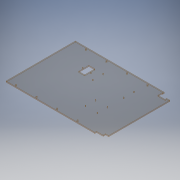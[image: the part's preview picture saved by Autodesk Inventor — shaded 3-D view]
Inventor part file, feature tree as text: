
AUTODESK INVENTOR PART (.ipt)
format: ipt  version: 2019.4 (Build 234330000, 330)  size: 210,944 bytes
history: native  units: mm
features: sketch x6, extrude x5
ambient origin geometry x8: Origin, YZ Plane, XZ Plane, XY Plane, X Axis, Y Axis, Z Axis, Center Point
bodies: Solid1 (feature_tree)
feature tree (11):
  extrude  "Extrusion1"  Depth=337.83mm
  extrude  "Extrusion2"  Depth=20.0mm
  extrude  "Extrusion3"  Depth=8.0mm
  sketch  "Sketch5"  dims[d7=90.0deg d8=12.0mm]
  extrude  "Extrusion4"  Depth=12.0mm
  extrude  "Extrusion5"  Depth=5.0mm TaperAngle=0.0deg
  sketch  "Sketch1"  dims[d0=480.0mm d1=337.83mm]
  sketch  "Sketch2"  dims[d2=5.0mm d3=0.0mm d4=20.0mm]
  sketch  "Sketch4"  dims[d5=15.0mm d6=8.0mm]
  sketch  "Sketch8"  dims[d9=32.0mm d10=5.0mm d11=0.0mm]
  sketch  "Sketch9"  dims[d14=40.0mm d15=8.732mm d16=5.5mm d17=40.0mm d19=100.0mm d20=10.0mm d22=10.0mm d24=60.0mm d25=8.732mm d26=5.5mm d27=40.0mm d29=100.0mm d30=10.0mm d32=10.0mm d34=10.0mm d35=0.0mm d36=480.0mm d37=339.0mm d38=35.0mm d39=20.0mm d40=10.0mm d41=0.0mm d42=4.0mm d43=70.0mm d44=125.0mm d45=20.0mm d47=50.0mm d48=20.0mm d50=150.0mm d53=40.0mm d54=180.0deg d55=15.0mm d56=15.0mm d57=29.0mm d58=50.0mm d59=5.5mm d60=5.5mm d61=3.5mm d62=3.5mm d63=3.5mm d64=90.0mm d65=125.0mm d66=20.0mm d68=58.0mm d69=20.0mm d71=49.0mm d74=10.0mm d75=0.0mm]
